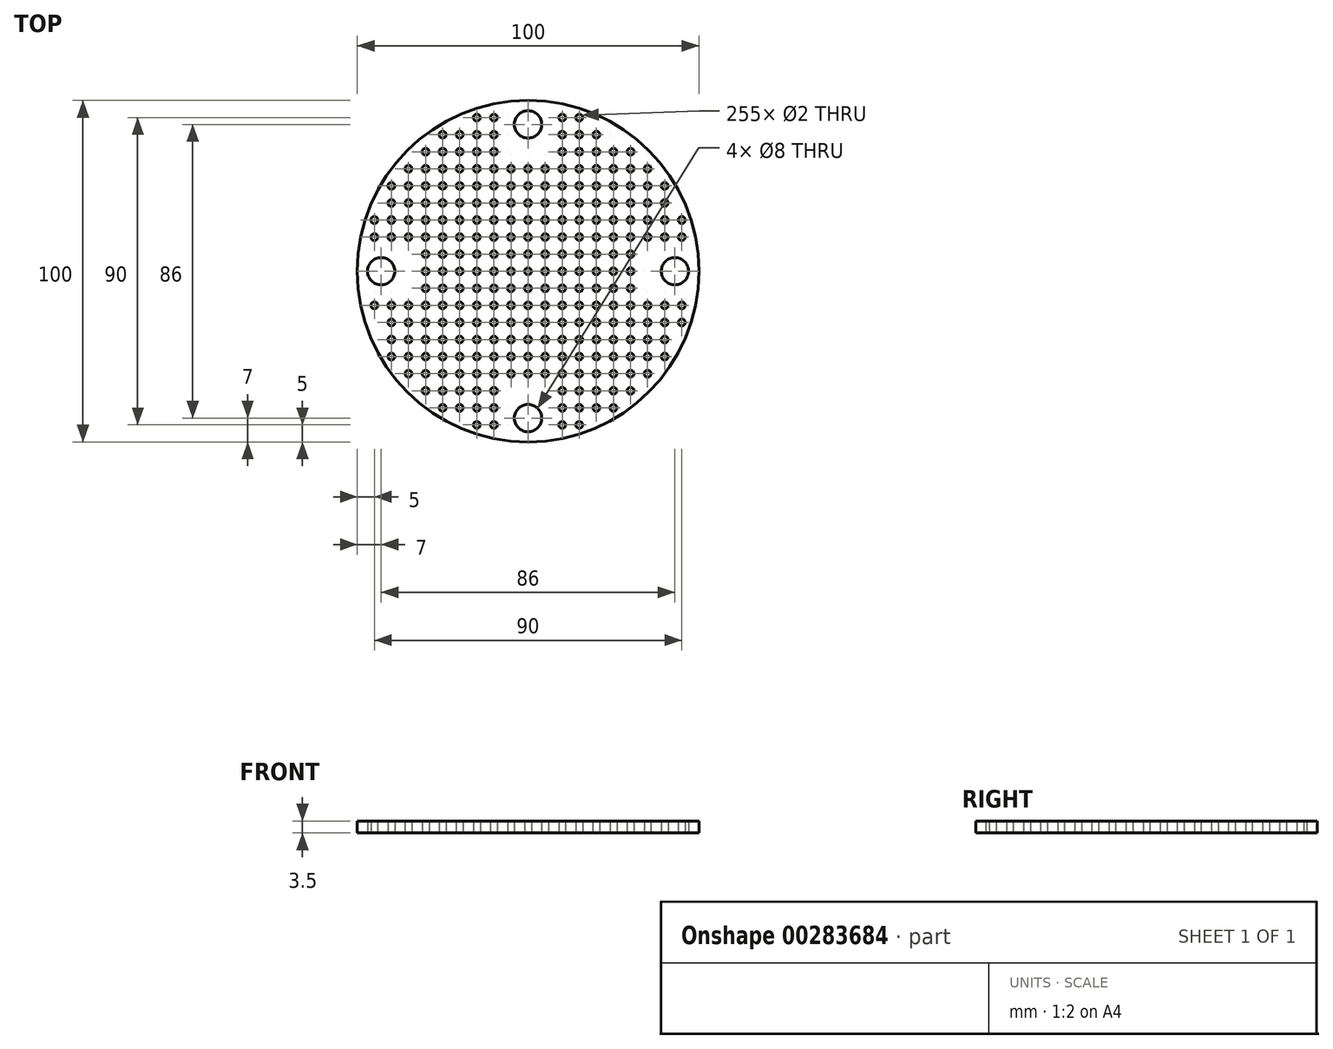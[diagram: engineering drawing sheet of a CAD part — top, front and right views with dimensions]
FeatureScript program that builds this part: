
annotation { "Feature Type Name" : "Feature", "Feature Type Description" : "" }
export const myFeature = defineFeature(function(context is Context, id is Id, definition is map)
    precondition{}
    {
        {
            var Q0;
            Q0=qCreatedBy(makeId("Top.planeOp"),FACE);
            var sketch = newSketch(context, id + "F0", { "sketchPlane" : qUnion([Q0])});
            skCircle(sketch, "E0", {"center": v(0, 0) * mm, "radius": 50 * mm});
            skCircle(sketch, "E1", {"center": v(0, -43) * mm, "radius": 4 * mm});
            skCircle(sketch, "E2.1.0", {"center": v(-43, 0) * mm, "radius": 4 * mm});
            skCircle(sketch, "E2.2.0", {"center": v(0, 43) * mm, "radius": 4 * mm});
            skCircle(sketch, "E2.3.0", {"center": v(43, 0) * mm, "radius": 4 * mm});
            skLineSegment(sketch, "E2.anchor1", {"start": v(0, 0) * mm, "end": v(0, -43) * mm, "construction": true});
            skLineSegment(sketch, "E2.anchor2", {"start": v(0, 0) * mm, "end": v(43, 0) * mm, "construction": true});
            skCircle(sketch, "E3.1.8.0", {"center": v(-45, -10) * mm, "radius": 1 * mm});
            skCircle(sketch, "E3.1.12.0", {"center": v(-45, 10) * mm, "radius": 1 * mm});
            skCircle(sketch, "E3.1.13.0", {"center": v(-45, 15) * mm, "radius": 1 * mm});
            skCircle(sketch, "E3.2.5.0", {"center": v(-40, -25) * mm, "radius": 1 * mm});
            skCircle(sketch, "E3.2.6.0", {"center": v(-40, -20) * mm, "radius": 1 * mm});
            skCircle(sketch, "E3.2.7.0", {"center": v(-40, -15) * mm, "radius": 1 * mm});
            skCircle(sketch, "E3.2.8.0", {"center": v(-40, -10) * mm, "radius": 1 * mm});
            skCircle(sketch, "E3.2.12.0", {"center": v(-40, 10) * mm, "radius": 1 * mm});
            skCircle(sketch, "E3.2.13.0", {"center": v(-40, 15) * mm, "radius": 1 * mm});
            skCircle(sketch, "E3.2.14.0", {"center": v(-40, 20) * mm, "radius": 1 * mm});
            skCircle(sketch, "E3.3.4.0", {"center": v(-35, -30) * mm, "radius": 1 * mm});
            skCircle(sketch, "E3.3.5.0", {"center": v(-35, -25) * mm, "radius": 1 * mm});
            skCircle(sketch, "E3.3.6.0", {"center": v(-35, -20) * mm, "radius": 1 * mm});
            skCircle(sketch, "E3.3.7.0", {"center": v(-35, -15) * mm, "radius": 1 * mm});
            skCircle(sketch, "E3.3.8.0", {"center": v(-35, -10) * mm, "radius": 1 * mm});
            skCircle(sketch, "E3.3.12.0", {"center": v(-35, 10) * mm, "radius": 1 * mm});
            skCircle(sketch, "E3.3.13.0", {"center": v(-35, 15) * mm, "radius": 1 * mm});
            skCircle(sketch, "E3.3.14.0", {"center": v(-35, 20) * mm, "radius": 1 * mm});
            skCircle(sketch, "E3.4.3.0", {"center": v(-30, -35) * mm, "radius": 1 * mm});
            skCircle(sketch, "E3.4.4.0", {"center": v(-30, -30) * mm, "radius": 1 * mm});
            skCircle(sketch, "E3.4.5.0", {"center": v(-30, -25) * mm, "radius": 1 * mm});
            skCircle(sketch, "E3.4.6.0", {"center": v(-30, -20) * mm, "radius": 1 * mm});
            skCircle(sketch, "E3.4.7.0", {"center": v(-30, -15) * mm, "radius": 1 * mm});
            skCircle(sketch, "E3.4.8.0", {"center": v(-30, -10) * mm, "radius": 1 * mm});
            skCircle(sketch, "E3.4.9.0", {"center": v(-30, -5) * mm, "radius": 1 * mm});
            skCircle(sketch, "E3.4.10.0", {"center": v(-30, 0) * mm, "radius": 1 * mm});
            skCircle(sketch, "E3.4.11.0", {"center": v(-30, 5) * mm, "radius": 1 * mm});
            skCircle(sketch, "E3.4.12.0", {"center": v(-30, 10) * mm, "radius": 1 * mm});
            skCircle(sketch, "E3.4.13.0", {"center": v(-30, 15) * mm, "radius": 1 * mm});
            skCircle(sketch, "E3.4.14.0", {"center": v(-30, 20) * mm, "radius": 1 * mm});
            skCircle(sketch, "E3.5.2.0", {"center": v(-25, -40) * mm, "radius": 1 * mm});
            skCircle(sketch, "E3.5.3.0", {"center": v(-25, -35) * mm, "radius": 1 * mm});
            skCircle(sketch, "E3.5.4.0", {"center": v(-25, -30) * mm, "radius": 1 * mm});
            skCircle(sketch, "E3.5.5.0", {"center": v(-25, -25) * mm, "radius": 1 * mm});
            skCircle(sketch, "E3.5.6.0", {"center": v(-25, -20) * mm, "radius": 1 * mm});
            skCircle(sketch, "E3.5.7.0", {"center": v(-25, -15) * mm, "radius": 1 * mm});
            skCircle(sketch, "E3.5.8.0", {"center": v(-25, -10) * mm, "radius": 1 * mm});
            skCircle(sketch, "E3.5.9.0", {"center": v(-25, -5) * mm, "radius": 1 * mm});
            skCircle(sketch, "E3.5.10.0", {"center": v(-25, 0) * mm, "radius": 1 * mm});
            skCircle(sketch, "E3.5.11.0", {"center": v(-25, 5) * mm, "radius": 1 * mm});
            skCircle(sketch, "E3.5.12.0", {"center": v(-25, 10) * mm, "radius": 1 * mm});
            skCircle(sketch, "E3.5.13.0", {"center": v(-25, 15) * mm, "radius": 1 * mm});
            skCircle(sketch, "E3.5.14.0", {"center": v(-25, 20) * mm, "radius": 1 * mm});
            skCircle(sketch, "E3.6.2.0", {"center": v(-20, -40) * mm, "radius": 1 * mm});
            skCircle(sketch, "E3.6.3.0", {"center": v(-20, -35) * mm, "radius": 1 * mm});
            skCircle(sketch, "E3.6.4.0", {"center": v(-20, -30) * mm, "radius": 1 * mm});
            skCircle(sketch, "E3.6.5.0", {"center": v(-20, -25) * mm, "radius": 1 * mm});
            skCircle(sketch, "E3.6.6.0", {"center": v(-20, -20) * mm, "radius": 1 * mm});
            skCircle(sketch, "E3.6.7.0", {"center": v(-20, -15) * mm, "radius": 1 * mm});
            skCircle(sketch, "E3.6.8.0", {"center": v(-20, -10) * mm, "radius": 1 * mm});
            skCircle(sketch, "E3.6.9.0", {"center": v(-20, -5) * mm, "radius": 1 * mm});
            skCircle(sketch, "E3.6.10.0", {"center": v(-20, 0) * mm, "radius": 1 * mm});
            skCircle(sketch, "E3.6.11.0", {"center": v(-20, 5) * mm, "radius": 1 * mm});
            skCircle(sketch, "E3.6.12.0", {"center": v(-20, 10) * mm, "radius": 1 * mm});
            skCircle(sketch, "E3.6.13.0", {"center": v(-20, 15) * mm, "radius": 1 * mm});
            skCircle(sketch, "E3.6.14.0", {"center": v(-20, 20) * mm, "radius": 1 * mm});
            skCircle(sketch, "E3.7.2.0", {"center": v(-15, -40) * mm, "radius": 1 * mm});
            skCircle(sketch, "E3.7.3.0", {"center": v(-15, -35) * mm, "radius": 1 * mm});
            skCircle(sketch, "E3.7.4.0", {"center": v(-15, -30) * mm, "radius": 1 * mm});
            skCircle(sketch, "E3.7.5.0", {"center": v(-15, -25) * mm, "radius": 1 * mm});
            skCircle(sketch, "E3.7.6.0", {"center": v(-15, -20) * mm, "radius": 1 * mm});
            skCircle(sketch, "E3.7.7.0", {"center": v(-15, -15) * mm, "radius": 1 * mm});
            skCircle(sketch, "E3.7.8.0", {"center": v(-15, -10) * mm, "radius": 1 * mm});
            skCircle(sketch, "E3.7.9.0", {"center": v(-15, -5) * mm, "radius": 1 * mm});
            skCircle(sketch, "E3.7.10.0", {"center": v(-15, 0) * mm, "radius": 1 * mm});
            skCircle(sketch, "E3.7.11.0", {"center": v(-15, 5) * mm, "radius": 1 * mm});
            skCircle(sketch, "E3.7.12.0", {"center": v(-15, 10) * mm, "radius": 1 * mm});
            skCircle(sketch, "E3.7.13.0", {"center": v(-15, 15) * mm, "radius": 1 * mm});
            skCircle(sketch, "E3.7.14.0", {"center": v(-15, 20) * mm, "radius": 1 * mm});
            skCircle(sketch, "E3.8.2.0", {"center": v(-10, -40) * mm, "radius": 1 * mm});
            skCircle(sketch, "E3.8.3.0", {"center": v(-10, -35) * mm, "radius": 1 * mm});
            skCircle(sketch, "E3.8.4.0", {"center": v(-10, -30) * mm, "radius": 1 * mm});
            skCircle(sketch, "E3.8.5.0", {"center": v(-10, -25) * mm, "radius": 1 * mm});
            skCircle(sketch, "E3.8.6.0", {"center": v(-10, -20) * mm, "radius": 1 * mm});
            skCircle(sketch, "E3.8.7.0", {"center": v(-10, -15) * mm, "radius": 1 * mm});
            skCircle(sketch, "E3.8.8.0", {"center": v(-10, -10) * mm, "radius": 1 * mm});
            skCircle(sketch, "E3.8.9.0", {"center": v(-10, -5) * mm, "radius": 1 * mm});
            skCircle(sketch, "E3.8.10.0", {"center": v(-10, 0) * mm, "radius": 1 * mm});
            skCircle(sketch, "E3.8.11.0", {"center": v(-10, 5) * mm, "radius": 1 * mm});
            skCircle(sketch, "E3.8.12.0", {"center": v(-10, 10) * mm, "radius": 1 * mm});
            skCircle(sketch, "E3.8.13.0", {"center": v(-10, 15) * mm, "radius": 1 * mm});
            skCircle(sketch, "E3.8.14.0", {"center": v(-10, 20) * mm, "radius": 1 * mm});
            skCircle(sketch, "E3.9.4.0", {"center": v(-5, -30) * mm, "radius": 1 * mm});
            skCircle(sketch, "E3.9.5.0", {"center": v(-5, -25) * mm, "radius": 1 * mm});
            skCircle(sketch, "E3.9.6.0", {"center": v(-5, -20) * mm, "radius": 1 * mm});
            skCircle(sketch, "E3.9.7.0", {"center": v(-5, -15) * mm, "radius": 1 * mm});
            skCircle(sketch, "E3.9.8.0", {"center": v(-5, -10) * mm, "radius": 1 * mm});
            skCircle(sketch, "E3.9.9.0", {"center": v(-5, -5) * mm, "radius": 1 * mm});
            skCircle(sketch, "E3.9.10.0", {"center": v(-5, 0) * mm, "radius": 1 * mm});
            skCircle(sketch, "E3.9.11.0", {"center": v(-5, 5) * mm, "radius": 1 * mm});
            skCircle(sketch, "E3.9.12.0", {"center": v(-5, 10) * mm, "radius": 1 * mm});
            skCircle(sketch, "E3.9.13.0", {"center": v(-5, 15) * mm, "radius": 1 * mm});
            skCircle(sketch, "E3.9.14.0", {"center": v(-5, 20) * mm, "radius": 1 * mm});
            skCircle(sketch, "E3.10.4.0", {"center": v(0, -30) * mm, "radius": 1 * mm});
            skCircle(sketch, "E3.10.5.0", {"center": v(0, -25) * mm, "radius": 1 * mm});
            skCircle(sketch, "E3.10.6.0", {"center": v(0, -20) * mm, "radius": 1 * mm});
            skCircle(sketch, "E3.10.7.0", {"center": v(0, -15) * mm, "radius": 1 * mm});
            skCircle(sketch, "E3.10.8.0", {"center": v(0, -10) * mm, "radius": 1 * mm});
            skCircle(sketch, "E3.10.9.0", {"center": v(0, -5) * mm, "radius": 1 * mm});
            skCircle(sketch, "E3.10.10.0", {"center": v(0, 0) * mm, "radius": 1 * mm});
            skCircle(sketch, "E3.10.11.0", {"center": v(0, 5) * mm, "radius": 1 * mm});
            skCircle(sketch, "E3.10.12.0", {"center": v(0, 10) * mm, "radius": 1 * mm});
            skCircle(sketch, "E3.10.13.0", {"center": v(0, 15) * mm, "radius": 1 * mm});
            skCircle(sketch, "E3.10.14.0", {"center": v(0, 20) * mm, "radius": 1 * mm});
            skCircle(sketch, "E3.11.4.0", {"center": v(5, -30) * mm, "radius": 1 * mm});
            skCircle(sketch, "E3.11.5.0", {"center": v(5, -25) * mm, "radius": 1 * mm});
            skCircle(sketch, "E3.11.6.0", {"center": v(5, -20) * mm, "radius": 1 * mm});
            skCircle(sketch, "E3.11.7.0", {"center": v(5, -15) * mm, "radius": 1 * mm});
            skCircle(sketch, "E3.11.8.0", {"center": v(5, -10) * mm, "radius": 1 * mm});
            skCircle(sketch, "E3.11.9.0", {"center": v(5, -5) * mm, "radius": 1 * mm});
            skCircle(sketch, "E3.11.10.0", {"center": v(5, 0) * mm, "radius": 1 * mm});
            skCircle(sketch, "E3.11.11.0", {"center": v(5, 5) * mm, "radius": 1 * mm});
            skCircle(sketch, "E3.11.12.0", {"center": v(5, 10) * mm, "radius": 1 * mm});
            skCircle(sketch, "E3.11.13.0", {"center": v(5, 15) * mm, "radius": 1 * mm});
            skCircle(sketch, "E3.11.14.0", {"center": v(5, 20) * mm, "radius": 1 * mm});
            skCircle(sketch, "E3.12.1.0", {"center": v(10, -45) * mm, "radius": 1 * mm});
            skCircle(sketch, "E3.12.2.0", {"center": v(10, -40) * mm, "radius": 1 * mm});
            skCircle(sketch, "E3.12.3.0", {"center": v(10, -35) * mm, "radius": 1 * mm});
            skCircle(sketch, "E3.12.4.0", {"center": v(10, -30) * mm, "radius": 1 * mm});
            skCircle(sketch, "E3.12.5.0", {"center": v(10, -25) * mm, "radius": 1 * mm});
            skCircle(sketch, "E3.12.6.0", {"center": v(10, -20) * mm, "radius": 1 * mm});
            skCircle(sketch, "E3.12.7.0", {"center": v(10, -15) * mm, "radius": 1 * mm});
            skCircle(sketch, "E3.12.8.0", {"center": v(10, -10) * mm, "radius": 1 * mm});
            skCircle(sketch, "E3.12.9.0", {"center": v(10, -5) * mm, "radius": 1 * mm});
            skCircle(sketch, "E3.12.10.0", {"center": v(10, 0) * mm, "radius": 1 * mm});
            skCircle(sketch, "E3.12.11.0", {"center": v(10, 5) * mm, "radius": 1 * mm});
            skCircle(sketch, "E3.12.12.0", {"center": v(10, 10) * mm, "radius": 1 * mm});
            skCircle(sketch, "E3.12.13.0", {"center": v(10, 15) * mm, "radius": 1 * mm});
            skCircle(sketch, "E3.12.14.0", {"center": v(10, 20) * mm, "radius": 1 * mm});
            skCircle(sketch, "E3.13.1.0", {"center": v(15, -45) * mm, "radius": 1 * mm});
            skCircle(sketch, "E3.13.2.0", {"center": v(15, -40) * mm, "radius": 1 * mm});
            skCircle(sketch, "E3.13.3.0", {"center": v(15, -35) * mm, "radius": 1 * mm});
            skCircle(sketch, "E3.13.4.0", {"center": v(15, -30) * mm, "radius": 1 * mm});
            skCircle(sketch, "E3.13.5.0", {"center": v(15, -25) * mm, "radius": 1 * mm});
            skCircle(sketch, "E3.13.6.0", {"center": v(15, -20) * mm, "radius": 1 * mm});
            skCircle(sketch, "E3.13.7.0", {"center": v(15, -15) * mm, "radius": 1 * mm});
            skCircle(sketch, "E3.13.8.0", {"center": v(15, -10) * mm, "radius": 1 * mm});
            skCircle(sketch, "E3.13.9.0", {"center": v(15, -5) * mm, "radius": 1 * mm});
            skCircle(sketch, "E3.13.10.0", {"center": v(15, 0) * mm, "radius": 1 * mm});
            skCircle(sketch, "E3.13.11.0", {"center": v(15, 5) * mm, "radius": 1 * mm});
            skCircle(sketch, "E3.13.12.0", {"center": v(15, 10) * mm, "radius": 1 * mm});
            skCircle(sketch, "E3.13.13.0", {"center": v(15, 15) * mm, "radius": 1 * mm});
            skCircle(sketch, "E3.13.14.0", {"center": v(15, 20) * mm, "radius": 1 * mm});
            skCircle(sketch, "E3.14.2.0", {"center": v(20, -40) * mm, "radius": 1 * mm});
            skCircle(sketch, "E3.14.3.0", {"center": v(20, -35) * mm, "radius": 1 * mm});
            skCircle(sketch, "E3.14.4.0", {"center": v(20, -30) * mm, "radius": 1 * mm});
            skCircle(sketch, "E3.14.5.0", {"center": v(20, -25) * mm, "radius": 1 * mm});
            skCircle(sketch, "E3.14.6.0", {"center": v(20, -20) * mm, "radius": 1 * mm});
            skCircle(sketch, "E3.14.7.0", {"center": v(20, -15) * mm, "radius": 1 * mm});
            skCircle(sketch, "E3.14.8.0", {"center": v(20, -10) * mm, "radius": 1 * mm});
            skCircle(sketch, "E3.14.9.0", {"center": v(20, -5) * mm, "radius": 1 * mm});
            skCircle(sketch, "E3.14.10.0", {"center": v(20, 0) * mm, "radius": 1 * mm});
            skCircle(sketch, "E3.14.11.0", {"center": v(20, 5) * mm, "radius": 1 * mm});
            skCircle(sketch, "E3.14.12.0", {"center": v(20, 10) * mm, "radius": 1 * mm});
            skCircle(sketch, "E3.14.13.0", {"center": v(20, 15) * mm, "radius": 1 * mm});
            skCircle(sketch, "E3.14.14.0", {"center": v(20, 20) * mm, "radius": 1 * mm});
            skCircle(sketch, "E4.0.15.2", {"center": v(25, -40) * mm, "radius": 1 * mm});
            skCircle(sketch, "E4.0.15.3", {"center": v(25, -35) * mm, "radius": 1 * mm});
            skCircle(sketch, "E4.0.15.4", {"center": v(25, -30) * mm, "radius": 1 * mm});
            skCircle(sketch, "E4.0.15.5", {"center": v(25, -25) * mm, "radius": 1 * mm});
            skCircle(sketch, "E4.0.15.6", {"center": v(25, -20) * mm, "radius": 1 * mm});
            skCircle(sketch, "E4.0.15.7", {"center": v(25, -15) * mm, "radius": 1 * mm});
            skCircle(sketch, "E4.0.15.8", {"center": v(25, -10) * mm, "radius": 1 * mm});
            skCircle(sketch, "E4.0.15.9", {"center": v(25, -5) * mm, "radius": 1 * mm});
            skCircle(sketch, "E4.0.15.10", {"center": v(25, 0) * mm, "radius": 1 * mm});
            skCircle(sketch, "E4.0.15.11", {"center": v(25, 5) * mm, "radius": 1 * mm});
            skCircle(sketch, "E4.0.15.12", {"center": v(25, 10) * mm, "radius": 1 * mm});
            skCircle(sketch, "E4.0.15.13", {"center": v(25, 15) * mm, "radius": 1 * mm});
            skCircle(sketch, "E4.0.15.14", {"center": v(25, 20) * mm, "radius": 1 * mm});
            skCircle(sketch, "E4.0.16.3", {"center": v(30, -35) * mm, "radius": 1 * mm});
            skCircle(sketch, "E4.0.16.4", {"center": v(30, -30) * mm, "radius": 1 * mm});
            skCircle(sketch, "E4.0.16.5", {"center": v(30, -25) * mm, "radius": 1 * mm});
            skCircle(sketch, "E4.0.16.6", {"center": v(30, -20) * mm, "radius": 1 * mm});
            skCircle(sketch, "E4.0.16.7", {"center": v(30, -15) * mm, "radius": 1 * mm});
            skCircle(sketch, "E4.0.16.8", {"center": v(30, -10) * mm, "radius": 1 * mm});
            skCircle(sketch, "E4.0.16.9", {"center": v(30, -5) * mm, "radius": 1 * mm});
            skCircle(sketch, "E4.0.16.10", {"center": v(30, 0) * mm, "radius": 1 * mm});
            skCircle(sketch, "E4.0.16.11", {"center": v(30, 5) * mm, "radius": 1 * mm});
            skCircle(sketch, "E4.0.16.12", {"center": v(30, 10) * mm, "radius": 1 * mm});
            skCircle(sketch, "E4.0.16.13", {"center": v(30, 15) * mm, "radius": 1 * mm});
            skCircle(sketch, "E4.0.16.14", {"center": v(30, 20) * mm, "radius": 1 * mm});
            skCircle(sketch, "E4.0.17.4", {"center": v(35, -30) * mm, "radius": 1 * mm});
            skCircle(sketch, "E4.0.17.5", {"center": v(35, -25) * mm, "radius": 1 * mm});
            skCircle(sketch, "E4.0.17.6", {"center": v(35, -20) * mm, "radius": 1 * mm});
            skCircle(sketch, "E4.0.17.7", {"center": v(35, -15) * mm, "radius": 1 * mm});
            skCircle(sketch, "E4.0.17.8", {"center": v(35, -10) * mm, "radius": 1 * mm});
            skCircle(sketch, "E4.0.17.12", {"center": v(35, 10) * mm, "radius": 1 * mm});
            skCircle(sketch, "E4.0.17.13", {"center": v(35, 15) * mm, "radius": 1 * mm});
            skCircle(sketch, "E4.0.17.14", {"center": v(35, 20) * mm, "radius": 1 * mm});
            skCircle(sketch, "E4.0.18.5", {"center": v(40, -25) * mm, "radius": 1 * mm});
            skCircle(sketch, "E4.0.18.6", {"center": v(40, -20) * mm, "radius": 1 * mm});
            skCircle(sketch, "E4.0.18.7", {"center": v(40, -15) * mm, "radius": 1 * mm});
            skCircle(sketch, "E4.0.18.8", {"center": v(40, -10) * mm, "radius": 1 * mm});
            skCircle(sketch, "E4.0.18.12", {"center": v(40, 10) * mm, "radius": 1 * mm});
            skCircle(sketch, "E4.0.18.13", {"center": v(40, 15) * mm, "radius": 1 * mm});
            skCircle(sketch, "E4.0.18.14", {"center": v(40, 20) * mm, "radius": 1 * mm});
            skCircle(sketch, "E4.0.19.7", {"center": v(45, -15) * mm, "radius": 1 * mm});
            skCircle(sketch, "E4.0.19.8", {"center": v(45, -10) * mm, "radius": 1 * mm});
            skCircle(sketch, "E4.0.19.12", {"center": v(45, 10) * mm, "radius": 1 * mm});
            skCircle(sketch, "E4.0.19.13", {"center": v(45, 15) * mm, "radius": 1 * mm});
            skCircle(sketch, "E5.0.2.15", {"center": v(-40, 25) * mm, "radius": 1 * mm});
            skCircle(sketch, "E5.0.3.15", {"center": v(-35, 25) * mm, "radius": 1 * mm});
            skCircle(sketch, "E5.0.3.16", {"center": v(-35, 30) * mm, "radius": 1 * mm});
            skCircle(sketch, "E5.0.4.15", {"center": v(-30, 25) * mm, "radius": 1 * mm});
            skCircle(sketch, "E5.0.4.16", {"center": v(-30, 30) * mm, "radius": 1 * mm});
            skCircle(sketch, "E5.0.4.17", {"center": v(-30, 35) * mm, "radius": 1 * mm});
            skCircle(sketch, "E5.0.5.15", {"center": v(-25, 25) * mm, "radius": 1 * mm});
            skCircle(sketch, "E5.0.5.16", {"center": v(-25, 30) * mm, "radius": 1 * mm});
            skCircle(sketch, "E5.0.5.17", {"center": v(-25, 35) * mm, "radius": 1 * mm});
            skCircle(sketch, "E5.0.5.18", {"center": v(-25, 40) * mm, "radius": 1 * mm});
            skCircle(sketch, "E5.0.6.15", {"center": v(-20, 25) * mm, "radius": 1 * mm});
            skCircle(sketch, "E5.0.6.16", {"center": v(-20, 30) * mm, "radius": 1 * mm});
            skCircle(sketch, "E5.0.6.17", {"center": v(-20, 35) * mm, "radius": 1 * mm});
            skCircle(sketch, "E5.0.6.18", {"center": v(-20, 40) * mm, "radius": 1 * mm});
            skCircle(sketch, "E5.0.7.15", {"center": v(-15, 25) * mm, "radius": 1 * mm});
            skCircle(sketch, "E5.0.7.16", {"center": v(-15, 30) * mm, "radius": 1 * mm});
            skCircle(sketch, "E5.0.7.17", {"center": v(-15, 35) * mm, "radius": 1 * mm});
            skCircle(sketch, "E5.0.7.18", {"center": v(-15, 40) * mm, "radius": 1 * mm});
            skCircle(sketch, "E5.0.7.19", {"center": v(-15, 45) * mm, "radius": 1 * mm});
            skCircle(sketch, "E5.0.8.15", {"center": v(-10, 25) * mm, "radius": 1 * mm});
            skCircle(sketch, "E5.0.8.16", {"center": v(-10, 30) * mm, "radius": 1 * mm});
            skCircle(sketch, "E5.0.8.17", {"center": v(-10, 35) * mm, "radius": 1 * mm});
            skCircle(sketch, "E5.0.8.18", {"center": v(-10, 40) * mm, "radius": 1 * mm});
            skCircle(sketch, "E5.0.8.19", {"center": v(-10, 45) * mm, "radius": 1 * mm});
            skCircle(sketch, "E5.0.9.15", {"center": v(-5, 25) * mm, "radius": 1 * mm});
            skCircle(sketch, "E5.0.9.16", {"center": v(-5, 30) * mm, "radius": 1 * mm});
            skCircle(sketch, "E5.0.10.15", {"center": v(0, 25) * mm, "radius": 1 * mm});
            skCircle(sketch, "E5.0.10.16", {"center": v(0, 30) * mm, "radius": 1 * mm});
            skCircle(sketch, "E5.0.11.15", {"center": v(5, 25) * mm, "radius": 1 * mm});
            skCircle(sketch, "E5.0.11.16", {"center": v(5, 30) * mm, "radius": 1 * mm});
            skCircle(sketch, "E5.0.12.15", {"center": v(10, 25) * mm, "radius": 1 * mm});
            skCircle(sketch, "E5.0.12.16", {"center": v(10, 30) * mm, "radius": 1 * mm});
            skCircle(sketch, "E5.0.12.17", {"center": v(10, 35) * mm, "radius": 1 * mm});
            skCircle(sketch, "E5.0.12.18", {"center": v(10, 40) * mm, "radius": 1 * mm});
            skCircle(sketch, "E5.0.12.19", {"center": v(10, 45) * mm, "radius": 1 * mm});
            skCircle(sketch, "E5.0.13.15", {"center": v(15, 25) * mm, "radius": 1 * mm});
            skCircle(sketch, "E5.0.13.16", {"center": v(15, 30) * mm, "radius": 1 * mm});
            skCircle(sketch, "E5.0.13.17", {"center": v(15, 35) * mm, "radius": 1 * mm});
            skCircle(sketch, "E5.0.13.18", {"center": v(15, 40) * mm, "radius": 1 * mm});
            skCircle(sketch, "E5.0.13.19", {"center": v(15, 45) * mm, "radius": 1 * mm});
            skCircle(sketch, "E5.0.14.15", {"center": v(20, 25) * mm, "radius": 1 * mm});
            skCircle(sketch, "E5.0.14.16", {"center": v(20, 30) * mm, "radius": 1 * mm});
            skCircle(sketch, "E5.0.14.17", {"center": v(20, 35) * mm, "radius": 1 * mm});
            skCircle(sketch, "E5.0.14.18", {"center": v(20, 40) * mm, "radius": 1 * mm});
            skCircle(sketch, "E5.0.15.15", {"center": v(25, 25) * mm, "radius": 1 * mm});
            skCircle(sketch, "E5.0.15.16", {"center": v(25, 30) * mm, "radius": 1 * mm});
            skCircle(sketch, "E5.0.15.17", {"center": v(25, 35) * mm, "radius": 1 * mm});
            skCircle(sketch, "E5.0.16.15", {"center": v(30, 25) * mm, "radius": 1 * mm});
            skCircle(sketch, "E5.0.16.16", {"center": v(30, 30) * mm, "radius": 1 * mm});
            skCircle(sketch, "E5.0.16.17", {"center": v(30, 35) * mm, "radius": 1 * mm});
            skCircle(sketch, "E5.0.17.15", {"center": v(35, 25) * mm, "radius": 1 * mm});
            skCircle(sketch, "E5.0.17.16", {"center": v(35, 30) * mm, "radius": 1 * mm});
            skCircle(sketch, "E5.0.18.15", {"center": v(40, 25) * mm, "radius": 1 * mm});
            skCircle(sketch, "E6.12.1.0", {"center": v(-15, -45) * mm, "radius": 1 * mm});
            skCircle(sketch, "E6.13.1.0", {"center": v(-10, -45) * mm, "radius": 1 * mm});
            skSolve(sketch);
        }
        {
            var Q0;
            Q0=makeQuery(id+"F0.imprint","IMPRINT",FACE,{"disambiguationData":[TD([[makeQuery(id+"F0.imprint","IMPRINT",EDGE,{"derivedFrom":sQuery(id+"F0.wireOp",EDGE,"E0")}),1.0]])]});
            extrude(context, id + "F1", {"entities" : qUnion([Q0]), "depth" : 3.5 * mm});
        }
    });
